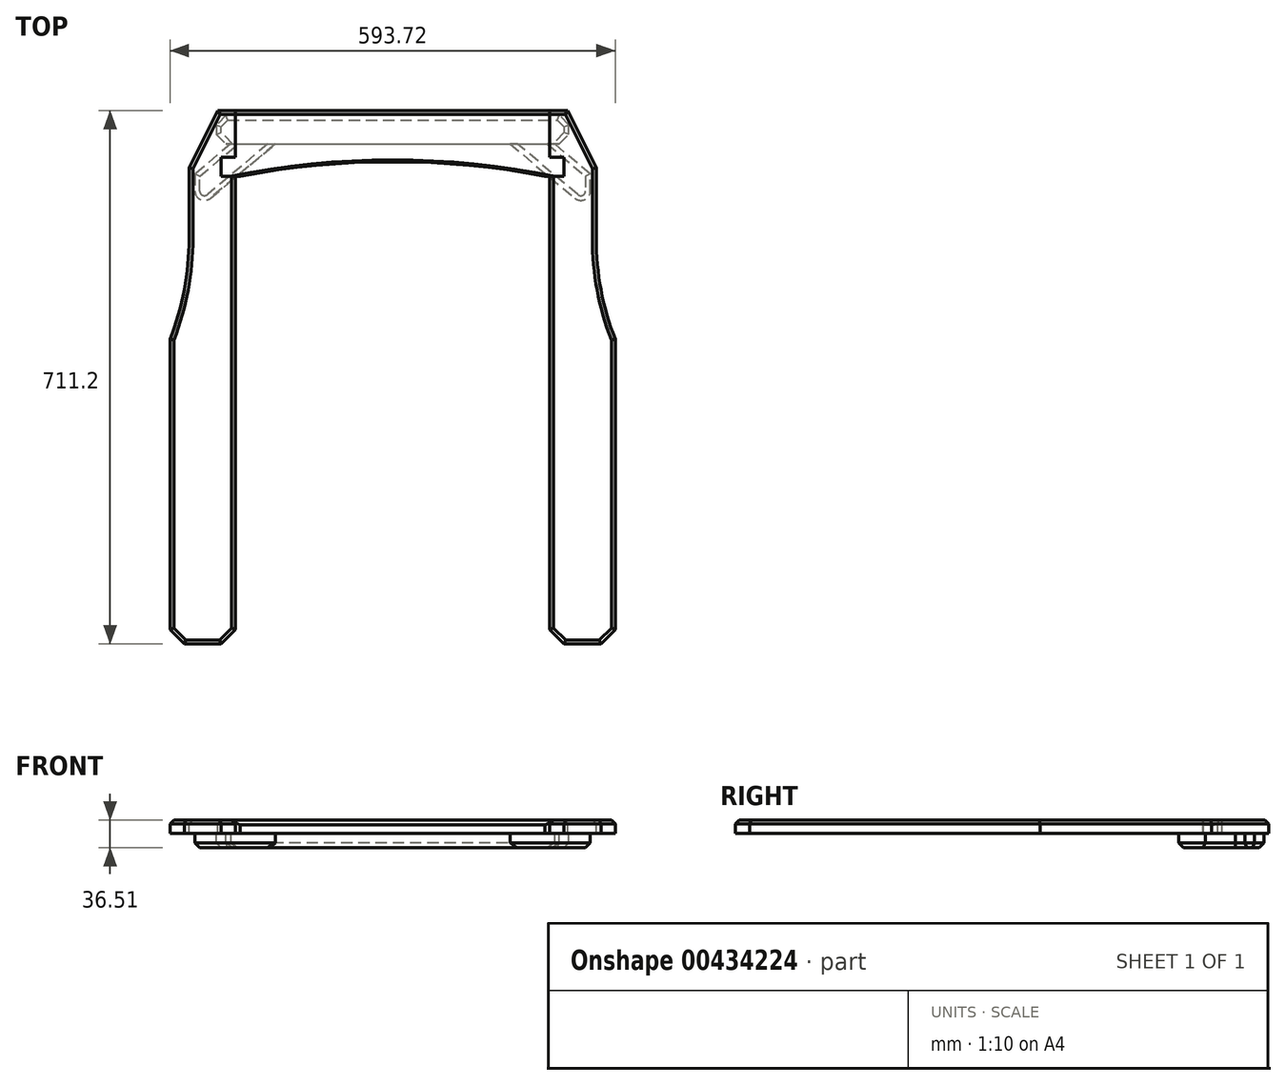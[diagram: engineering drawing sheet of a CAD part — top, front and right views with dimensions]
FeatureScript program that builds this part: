
annotation { "Feature Type Name" : "Feature", "Feature Type Description" : "" }
export const myFeature = defineFeature(function(context is Context, id is Id, definition is map)
    precondition{}
    {
        {
            var Q0;
            Q0=qCreatedBy(makeId("Top.planeOp"),FACE);
            var sketch = newSketch(context, id + "F0", { "sketchPlane" : qUnion([Q0])});
            skLineSegment(sketch, "E0.bottom", {"start": v(0, 0) * mm, "end": v(25.4, 0) * mm});
            skLineSegment(sketch, "E1", {"start": v(25.4, 18.53) * mm, "end": v(25.4, 0.79) * mm, "construction": true});
            skLineSegment(sketch, "E2", {"start": v(431.8, 17.8) * mm, "end": v(431.8, 0) * mm, "construction": true});
            skLineSegment(sketch, "E3", {"start": v(25.4, 0.79) * mm, "end": v(25.4, -24.2) * mm, "construction": true});
            skLineSegment(sketch, "E4", {"start": v(431.8, 0) * mm, "end": v(431.8, -25.28) * mm, "construction": true});
            skLineSegment(sketch, "E5", {"start": v(25.4, 0) * mm, "end": v(431.8, 0) * mm, "construction": true});
            skLineSegment(sketch, "E6", {"start": v(431.8, 0) * mm, "end": v(457.2, 0) * mm});
            skLineSegment(sketch, "E7", {"start": v(228.6, 19.05) * mm, "end": v(228.6, 0) * mm, "construction": true});
            skPoint(sketch, "E7.startSnap0", {"position": v(228.6, 0) * mm});
            skArc(sketch, "E8", {"start": v(431.8, 0) * mm, "mid": v(228.6, 19.05) * mm, "end": v(25.4, 0) * mm});
            skLineSegment(sketch, "E9", {"start": v(0, 0) * mm, "end": v(0, 25.4) * mm});
            skLineSegment(sketch, "E10", {"start": v(0, 25.4) * mm, "end": v(19.05, 25.4) * mm});
            skLineSegment(sketch, "E11", {"start": v(19.05, 25.4) * mm, "end": v(19.05, 87.31) * mm});
            skLineSegment(sketch, "E12", {"start": v(19.05, 87.31) * mm, "end": v(438.15, 87.31) * mm});
            skLineSegment(sketch, "E13", {"start": v(438.15, 87.31) * mm, "end": v(438.15, 25.4) * mm});
            skLineSegment(sketch, "E14", {"start": v(438.15, 25.4) * mm, "end": v(457.2, 25.4) * mm});
            skLineSegment(sketch, "E15", {"start": v(457.2, 25.4) * mm, "end": v(457.2, 0) * mm});
            skSolve(sketch);
        }
        {
            var Q0;
            Q0 = qSketchRegion(id + "F0", true);
            extrude(context, id + "F1", {"entities" : qUnion([Q0]), "depth" : 17.46 * mm});
        }
        {
            var Q0;
            Q0=makeQuery(id+"F1.opExtrude","CAP_EDGE",EDGE,{"disambiguationData":[OSD([sQuery(id+"F0.wireOp",EDGE,"E8")])],"isStart":false});
            chamfer(context, id + "F2", {"entities" : qUnion([Q0]), "chamferType" : ChamferType.TWO_OFFSETS, "width1" : 6.35 * mm, "oppositeDirection" : false, "width2" : 2.54 * mm, "tangentPropagation" : true});
        }
        {
            var Q0;
            Q0=makeQuery(id+"F1.opExtrude","CAP_FACE",FACE,{"disambiguationData":[OSD([sQuery(id+"F0.wireOp",EDGE,"E0.bottom"),sQuery(id+"F0.wireOp",EDGE,"E6"),sQuery(id+"F0.wireOp",EDGE,"E8"),sQuery(id+"F0.wireOp",EDGE,"E9"),sQuery(id+"F0.wireOp",EDGE,"E10"),sQuery(id+"F0.wireOp",EDGE,"E11"),sQuery(id+"F0.wireOp",EDGE,"E12"),sQuery(id+"F0.wireOp",EDGE,"E13"),sQuery(id+"F0.wireOp",EDGE,"E14"),sQuery(id+"F0.wireOp",EDGE,"E15")])],"isStart":false});
            var sketch = newSketch(context, id + "F3", { "sketchPlane" : qUnion([Q0])});
            skLineSegment(sketch, "E16", {"start": v(228.6, 119.18) * mm, "end": v(228.6, -123.03) * mm, "construction": true});
            skPoint(sketch, "E16.startSnap0", {"position": v(228.6, 87.31) * mm});
            skLineSegment(sketch, "E17", {"start": v(-4.76, 87.31) * mm, "end": v(-42.86, 11.11) * mm});
            skLineSegment(sketch, "E18", {"start": v(-42.86, 11.11) * mm, "end": v(-42.86, -83.27) * mm});
            skLineSegment(sketch, "E19", {"start": v(19.05, 25.4) * mm, "end": v(0, 25.4) * mm});
            skLineSegment(sketch, "E20", {"start": v(0, 25.4) * mm, "end": v(0, 0) * mm});
            skLineSegment(sketch, "E21", {"start": v(0, 0) * mm, "end": v(19.05, 0) * mm});
            skLineSegment(sketch, "E22", {"start": v(19.05, 87.31) * mm, "end": v(-4.76, 87.31) * mm});
            skLineSegment(sketch, "E23", {"start": v(19.05, 87.31) * mm, "end": v(19.05, 25.4) * mm});
            skLineSegment(sketch, "E24", {"start": v(19.05, 0) * mm, "end": v(19.05, -604.84) * mm});
            skLineSegment(sketch, "E25", {"start": v(-68.26, -604.84) * mm, "end": v(-49.21, -623.89) * mm});
            skLineSegment(sketch, "E26", {"start": v(-49.21, -623.89) * mm, "end": v(0, -623.89) * mm});
            skLineSegment(sketch, "E27", {"start": v(0, -623.89) * mm, "end": v(19.05, -604.84) * mm});
            skLineSegment(sketch, "E28", {"start": v(-68.26, -217.49) * mm, "end": v(-34.9, -217.49) * mm, "construction": true});
            skArc(sketch, "E29", {"start": v(-68.26, -217.49) * mm, "mid": v(-49.27, -151.57) * mm, "end": v(-42.86, -83.27) * mm});
            skLineSegment(sketch, "E30", {"start": v(-68.26, -217.49) * mm, "end": v(-68.26, -604.84) * mm});
            skLineSegment(sketch, "E31.MirrorCS", {"start": v(457.2, 0) * mm, "end": v(438.15, 0) * mm});
            skLineSegment(sketch, "E32.MirrorCS", {"start": v(457.2, 25.4) * mm, "end": v(457.2, 0) * mm});
            skLineSegment(sketch, "E33.MirrorCS", {"start": v(525.46, -604.84) * mm, "end": v(506.41, -623.89) * mm});
            skLineSegment(sketch, "E34.MirrorCS", {"start": v(457.2, -623.89) * mm, "end": v(438.15, -604.84) * mm});
            skLineSegment(sketch, "E35.MirrorCS", {"start": v(461.96, 87.31) * mm, "end": v(500.06, 11.11) * mm});
            skLineSegment(sketch, "E36.MirrorCS", {"start": v(438.15, 25.4) * mm, "end": v(457.2, 25.4) * mm});
            skLineSegment(sketch, "E37.MirrorCS", {"start": v(438.15, 87.31) * mm, "end": v(438.15, 25.4) * mm});
            skLineSegment(sketch, "E38.MirrorCS", {"start": v(438.15, 0) * mm, "end": v(438.15, -604.84) * mm});
            skLineSegment(sketch, "E39.MirrorCS", {"start": v(438.15, 87.31) * mm, "end": v(461.96, 87.31) * mm});
            skLineSegment(sketch, "E40.MirrorCS", {"start": v(500.06, 11.11) * mm, "end": v(500.06, -83.27) * mm});
            skLineSegment(sketch, "E41.MirrorCS", {"start": v(525.46, -217.49) * mm, "end": v(492.1, -217.49) * mm, "construction": true});
            skLineSegment(sketch, "E42.MirrorCS", {"start": v(506.41, -623.89) * mm, "end": v(457.2, -623.89) * mm});
            skLineSegment(sketch, "E43.MirrorCS", {"start": v(525.46, -217.49) * mm, "end": v(525.46, -604.84) * mm});
            skArc(sketch, "E44.MirrorCS", {"start": v(525.46, -217.49) * mm, "mid": v(506.47, -151.57) * mm, "end": v(500.06, -83.27) * mm});
            skSolve(sketch);
        }
        {
            var Q0;
            Q0 = qSketchRegion(id + "F3", true);
            extrude(context, id + "F4", {"entities" : qUnion([Q0]), "depth" : -17.46 * mm});
        }
        {
            var Q0;
            Q0=makeQuery(id+"F1.opExtrude","CAP_EDGE",EDGE,{"disambiguationData":[OSD([sQuery(id+"F0.wireOp",EDGE,"E12")])],"isStart":false});
            var Q1;
            Q1=makeQuery(id+"F4.opExtrude","CAP_EDGE",EDGE,{"disambiguationData":[OSD([sQuery(id+"F3.wireOp",EDGE,"E22")])],"isStart":true});
            var Q2;
            Q2=makeQuery(id+"F4.opExtrude","CAP_EDGE",EDGE,{"disambiguationData":[OSD([sQuery(id+"F3.wireOp",EDGE,"E17")])],"isStart":true});
            var Q3;
            Q3=makeQuery(id+"F4.opExtrude","CAP_EDGE",EDGE,{"disambiguationData":[OSD([sQuery(id+"F3.wireOp",EDGE,"E18")])],"isStart":true});
            var Q4;
            Q4=makeQuery(id+"F4.opExtrude","CAP_EDGE",EDGE,{"disambiguationData":[OSD([sQuery(id+"F3.wireOp",EDGE,"E30")])],"isStart":true});
            var Q5;
            Q5=makeQuery(id+"F4.opExtrude","CAP_EDGE",EDGE,{"disambiguationData":[OSD([sQuery(id+"F3.wireOp",EDGE,"E25")])],"isStart":true});
            var Q6;
            Q6=makeQuery(id+"F4.opExtrude","CAP_EDGE",EDGE,{"disambiguationData":[OSD([sQuery(id+"F3.wireOp",EDGE,"E26")])],"isStart":true});
            var Q7;
            Q7=makeQuery(id+"F4.opExtrude","CAP_EDGE",EDGE,{"disambiguationData":[OSD([sQuery(id+"F3.wireOp",EDGE,"E27")])],"isStart":true});
            var Q8;
            Q8=makeQuery(id+"F4.opExtrude","CAP_EDGE",EDGE,{"disambiguationData":[OSD([sQuery(id+"F3.wireOp",EDGE,"E24")])],"isStart":true});
            var Q9;
            Q9=makeQuery(id+"F4.opExtrude","CAP_EDGE",EDGE,{"disambiguationData":[OSD([sQuery(id+"F3.wireOp",EDGE,"E39.MirrorCS")])],"isStart":true});
            var Q10;
            Q10=makeQuery(id+"F4.opExtrude","CAP_EDGE",EDGE,{"disambiguationData":[OSD([sQuery(id+"F3.wireOp",EDGE,"E35.MirrorCS")])],"isStart":true});
            var Q11;
            Q11=makeQuery(id+"F4.opExtrude","CAP_EDGE",EDGE,{"disambiguationData":[OSD([sQuery(id+"F3.wireOp",EDGE,"E40.MirrorCS")])],"isStart":true});
            var Q12;
            Q12=makeQuery(id+"F4.opExtrude","CAP_EDGE",EDGE,{"disambiguationData":[OSD([sQuery(id+"F3.wireOp",EDGE,"E44.MirrorCS")])],"isStart":true});
            var Q13;
            Q13=makeQuery(id+"F4.opExtrude","CAP_EDGE",EDGE,{"disambiguationData":[OSD([sQuery(id+"F3.wireOp",EDGE,"E43.MirrorCS")])],"isStart":true});
            var Q14;
            Q14=makeQuery(id+"F4.opExtrude","CAP_EDGE",EDGE,{"disambiguationData":[OSD([sQuery(id+"F3.wireOp",EDGE,"E33.MirrorCS")])],"isStart":true});
            var Q15;
            Q15=makeQuery(id+"F4.opExtrude","CAP_EDGE",EDGE,{"disambiguationData":[OSD([sQuery(id+"F3.wireOp",EDGE,"E42.MirrorCS")])],"isStart":true});
            var Q16;
            Q16=makeQuery(id+"F4.opExtrude","CAP_EDGE",EDGE,{"disambiguationData":[OSD([sQuery(id+"F3.wireOp",EDGE,"E34.MirrorCS")])],"isStart":true});
            var Q17;
            Q17=makeQuery(id+"F4.opExtrude","CAP_EDGE",EDGE,{"disambiguationData":[OSD([sQuery(id+"F3.wireOp",EDGE,"E38.MirrorCS")])],"isStart":true});
            chamfer(context, id + "F5", {"entities" : qUnion([Q0, Q1, Q2, Q3, Q4, Q5, Q6, Q7, Q8, Q9, Q10, Q11, Q12, Q13, Q14, Q15, Q16, Q17]), "width" : 5.08 * mm, "tangentPropagation" : true});
        }
        {
            var Q0;
            Q0=makeQuery(id+"F1.opExtrude","CAP_FACE",FACE,{"disambiguationData":[OSD([sQuery(id+"F0.wireOp",EDGE,"E0.bottom"),sQuery(id+"F0.wireOp",EDGE,"E6"),sQuery(id+"F0.wireOp",EDGE,"E8"),sQuery(id+"F0.wireOp",EDGE,"E9"),sQuery(id+"F0.wireOp",EDGE,"E10"),sQuery(id+"F0.wireOp",EDGE,"E11"),sQuery(id+"F0.wireOp",EDGE,"E12"),sQuery(id+"F0.wireOp",EDGE,"E13"),sQuery(id+"F0.wireOp",EDGE,"E14"),sQuery(id+"F0.wireOp",EDGE,"E15")])],"isStart":true});
            var sketch = newSketch(context, id + "F6", { "sketchPlane" : qUnion([Q0])});
            skLineSegment(sketch, "E45", {"start": v(450.85, -80.96) * mm, "end": v(6.35, -80.96) * mm});
            skLineSegment(sketch, "E46", {"start": v(-6.35, -68.26) * mm, "end": v(-6.35, -55.56) * mm});
            skLineSegment(sketch, "E47", {"start": v(6.35, -42.86) * mm, "end": v(450.85, -42.86) * mm});
            skLineSegment(sketch, "E48", {"start": v(463.55, -55.56) * mm, "end": v(463.55, -68.26) * mm});
            skLineSegment(sketch, "E49", {"start": v(450.85, -80.96) * mm, "end": v(463.55, -68.26) * mm});
            skLineSegment(sketch, "E50", {"start": v(-6.35, -68.26) * mm, "end": v(6.35, -80.96) * mm});
            skLineSegment(sketch, "E51", {"start": v(450.85, -42.86) * mm, "end": v(463.55, -55.56) * mm});
            skLineSegment(sketch, "E52", {"start": v(-6.35, -55.56) * mm, "end": v(6.35, -42.86) * mm});
            skSolve(sketch);
        }
        {
            var Q0;
            Q0 = qSketchRegion(id + "F6", true);
            extrude(context, id + "F7", {"entities" : qUnion([Q0]), "depth" : 19.05 * mm});
        }
        {
            var Q0;
            Q0=makeQuery(id+"F7.opExtrude","CAP_FACE",FACE,{"disambiguationData":[OSD([sQuery(id+"F6.wireOp",EDGE,"E45"),sQuery(id+"F6.wireOp",EDGE,"E46"),sQuery(id+"F6.wireOp",EDGE,"E47"),sQuery(id+"F6.wireOp",EDGE,"E48"),sQuery(id+"F6.wireOp",EDGE,"E49")])],"isStart":false});
            var sketch = newSketch(context, id + "F8", { "sketchPlane" : qUnion([Q0])});
            skLineSegment(sketch, "E53", {"start": v(385.23, -42.86) * mm, "end": v(471.38, 29.43) * mm});
            skLineSegment(sketch, "E54", {"start": v(492.24, 19.7) * mm, "end": v(492.24, -2.8) * mm});
            skLineSegment(sketch, "E55", {"start": v(492.24, -2.8) * mm, "end": v(444.5, -42.86) * mm});
            skLineSegment(sketch, "E56", {"start": v(444.5, -42.86) * mm, "end": v(385.23, -42.86) * mm});
            skLineSegment(sketch, "E57", {"start": v(228.6, -80.96) * mm, "end": v(228.6, -42.86) * mm, "construction": true});
            skLineSegment(sketch, "E58.MirrorCS", {"start": v(-35.04, -2.8) * mm, "end": v(12.7, -42.86) * mm});
            skLineSegment(sketch, "E59.MirrorCS", {"start": v(12.7, -42.86) * mm, "end": v(71.97, -42.86) * mm});
            skLineSegment(sketch, "E60.MirrorCS", {"start": v(71.97, -42.86) * mm, "end": v(-14.18, 29.43) * mm});
            skLineSegment(sketch, "E61.MirrorCS", {"start": v(-35.04, 19.7) * mm, "end": v(-35.04, -2.8) * mm});
            skPoint(sketch, "E62.visualSharp", {"position": v(492.24, 46.93) * mm});
            skArc(sketch, "E62.filletArc", {"start": v(492.24, 19.7) * mm, "mid": v(484.91, 31.2) * mm, "end": v(471.38, 29.43) * mm});
            skArc(sketch, "E63.MirrorCS", {"start": v(-35.04, 19.7) * mm, "mid": v(-27.71, 31.2) * mm, "end": v(-14.18, 29.43) * mm});
            skLineSegment(sketch, "E64", {"start": v(492.24, 19.7) * mm, "end": v(492.24, 46.93) * mm, "construction": true});
            skLineSegment(sketch, "E65", {"start": v(492.24, 46.93) * mm, "end": v(471.38, 29.43) * mm, "construction": true});
            skSolve(sketch);
        }
        {
            var Q0;
            Q0 = qSketchRegion(id + "F8", true);
            extrude(context, id + "F9", {"entities" : qUnion([Q0]), "depth" : -19.05 * mm});
        }
        {
            var Q0;
            Q0=makeQuery(id+"F9.opExtrude","CAP_EDGE",EDGE,{"disambiguationData":[OSD([sQuery(id+"F8.wireOp",EDGE,"E55")])],"isStart":true});
            var Q1;
            Q1=makeQuery(id+"F9.opExtrude","CAP_EDGE",EDGE,{"disambiguationData":[OSD([sQuery(id+"F8.wireOp",EDGE,"E54")])],"isStart":true});
            var Q2;
            Q2=makeQuery(id+"F9.opExtrude","CAP_EDGE",EDGE,{"disambiguationData":[OSD([sQuery(id+"F8.wireOp",EDGE,"E62.filletArc")])],"isStart":true});
            var Q3;
            Q3=makeQuery(id+"F9.opExtrude","CAP_EDGE",EDGE,{"disambiguationData":[OSD([sQuery(id+"F8.wireOp",EDGE,"E60.MirrorCS")])],"isStart":true});
            var Q4;
            Q4=makeQuery(id+"F9.opExtrude","CAP_EDGE",EDGE,{"disambiguationData":[OSD([sQuery(id+"F8.wireOp",EDGE,"E63.MirrorCS")])],"isStart":true});
            var Q5;
            Q5=makeQuery(id+"F9.opExtrude","CAP_EDGE",EDGE,{"disambiguationData":[OSD([sQuery(id+"F8.wireOp",EDGE,"E58.MirrorCS")])],"isStart":true});
            var Q6;
            Q6=makeQuery(id+"F7.opExtrude","CAP_EDGE",EDGE,{"disambiguationData":[OSD([sQuery(id+"F6.wireOp",EDGE,"E46")])],"isStart":false});
            var Q7;
            Q7=makeQuery(id+"F7.opExtrude","CAP_EDGE",EDGE,{"disambiguationData":[OSD([sQuery(id+"F6.wireOp",EDGE,"E50")])],"isStart":false});
            var Q8;
            Q8=makeQuery(id+"F7.opExtrude","CAP_EDGE",EDGE,{"disambiguationData":[OSD([sQuery(id+"F6.wireOp",EDGE,"E45")])],"isStart":false});
            var Q9;
            Q9=makeQuery(id+"F7.opExtrude","CAP_EDGE",EDGE,{"disambiguationData":[OSD([sQuery(id+"F6.wireOp",EDGE,"E49")])],"isStart":false});
            var Q10;
            Q10=makeQuery(id+"F7.opExtrude","CAP_EDGE",EDGE,{"disambiguationData":[OSD([sQuery(id+"F6.wireOp",EDGE,"E48")])],"isStart":false});
            var Q11;
            Q11=makeQuery(id+"F7.opExtrude","CAP_EDGE",EDGE,{"disambiguationData":[OSD([sQuery(id+"F6.wireOp",EDGE,"E51")])],"isStart":false});
            var Q12;
            Q12=makeQuery(id+"F7.opExtrude","CAP_EDGE",EDGE,{"disambiguationData":[OSD([sQuery(id+"F6.wireOp",EDGE,"E52")])],"isStart":false});
            chamfer(context, id + "F10", {"entities" : qUnion([Q0, Q1, Q2, Q3, Q4, Q5, Q6, Q7, Q8, Q9, Q10, Q11, Q12]), "width" : 6.35 * mm, "tangentPropagation" : true});
        }
    });
